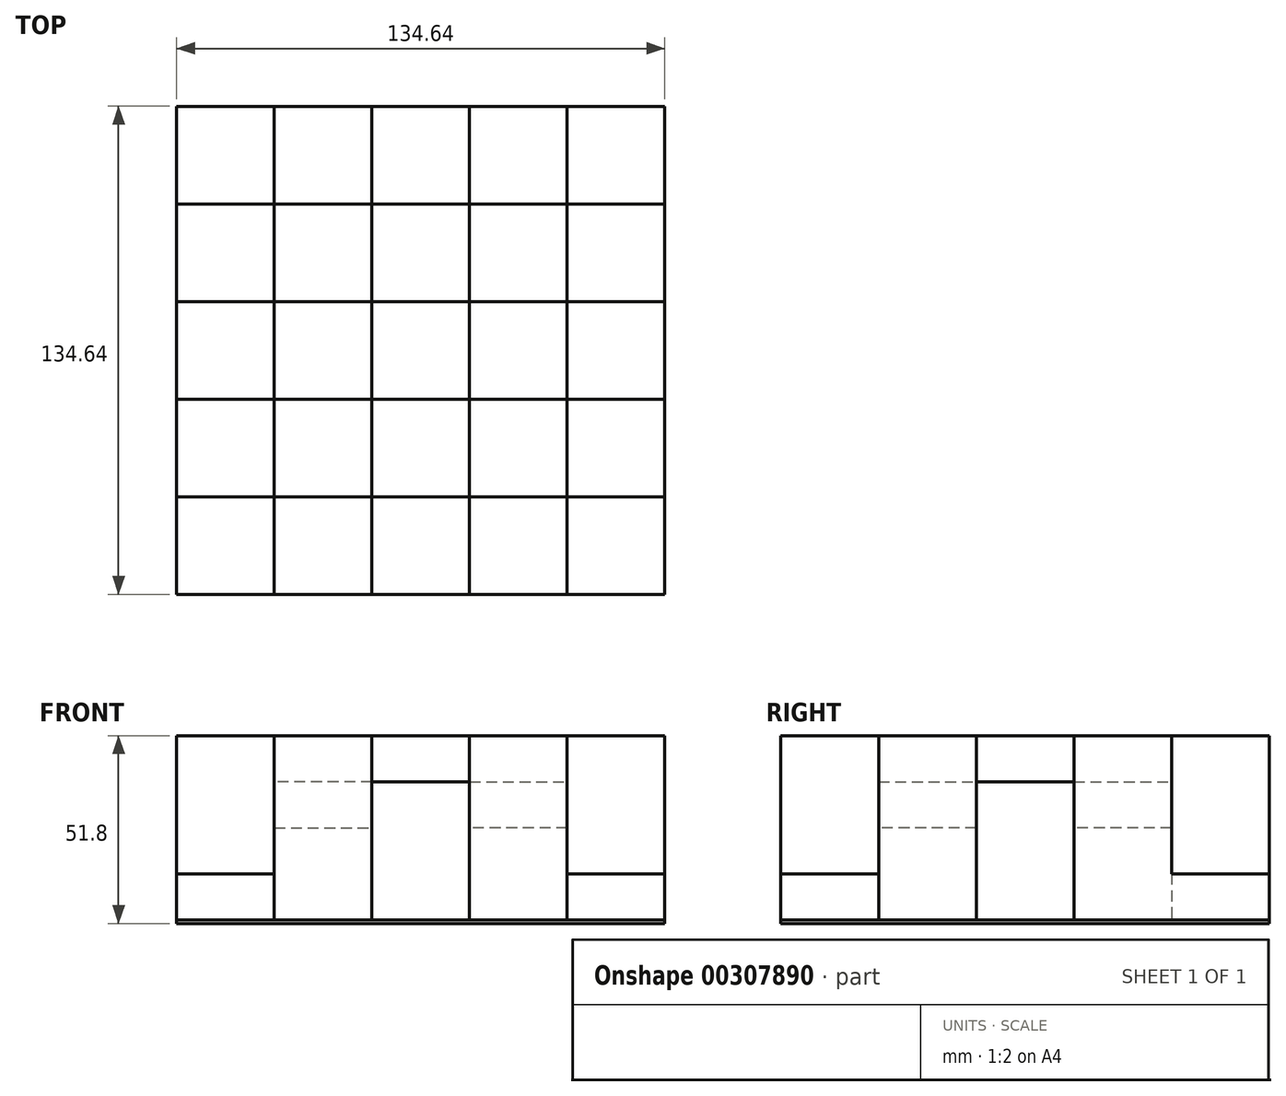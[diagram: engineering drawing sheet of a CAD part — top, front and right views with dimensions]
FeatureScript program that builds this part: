
annotation { "Feature Type Name" : "Feature", "Feature Type Description" : "" }
export const myFeature = defineFeature(function(context is Context, id is Id, definition is map)
    precondition{}
    {
        {
            var Q0;
            Q0=qCreatedBy(makeId("Top.planeOp"),FACE);
            var sketch = newSketch(context, id + "F0", { "sketchPlane" : qUnion([Q0])});
            skLineSegment(sketch, "E0.bottom", {"start": v(-67.32, 67.32) * mm, "end": v(-40.4, 67.32) * mm});
            skLineSegment(sketch, "E0.top", {"start": v(-67.32, -67.32) * mm, "end": v(67.32, -67.32) * mm});
            skLineSegment(sketch, "E0.left", {"start": v(-67.32, 67.32) * mm, "end": v(-67.32, -67.32) * mm});
            skLineSegment(sketch, "E0.right", {"start": v(67.32, 67.32) * mm, "end": v(67.32, -67.32) * mm});
            skPoint(sketch, "E0.middle", {"position": v(0, 0) * mm});
            skLineSegment(sketch, "E1", {"start": v(-40.4, 67.32) * mm, "end": v(-40.4, -67.32) * mm});
            skLineSegment(sketch, "E2", {"start": v(-13.46, 67.32) * mm, "end": v(-13.46, -67.32) * mm});
            skLineSegment(sketch, "E3", {"start": v(13.46, -67.32) * mm, "end": v(13.46, 67.32) * mm});
            skLineSegment(sketch, "E4", {"start": v(40.4, 67.32) * mm, "end": v(40.4, -67.32) * mm});
            skLineSegment(sketch, "E5", {"start": v(-40.4, 67.32) * mm, "end": v(-13.46, 67.32) * mm});
            skLineSegment(sketch, "E6", {"start": v(-13.46, 67.32) * mm, "end": v(13.46, 67.32) * mm});
            skLineSegment(sketch, "E7", {"start": v(13.46, 67.32) * mm, "end": v(40.4, 67.32) * mm});
            skLineSegment(sketch, "E8", {"start": v(40.4, 67.32) * mm, "end": v(67.32, 67.32) * mm});
            skLineSegment(sketch, "E9.1.1", {"start": v(67.32, 40.4) * mm, "end": v(-67.32, 40.4) * mm});
            skLineSegment(sketch, "E9.1.2", {"start": v(67.32, 13.46) * mm, "end": v(-67.32, 13.46) * mm});
            skLineSegment(sketch, "E9.1.3", {"start": v(-67.32, -13.46) * mm, "end": v(67.32, -13.46) * mm});
            skLineSegment(sketch, "E9.1.4", {"start": v(67.32, -40.4) * mm, "end": v(-67.32, -40.4) * mm});
            skLineSegment(sketch, "E9.anchor1", {"start": v(0, 0) * mm, "end": v(-40.4, -67.32) * mm, "construction": true});
            skLineSegment(sketch, "E9.anchor2", {"start": v(0, 0) * mm, "end": v(-67.32, 40.4) * mm, "construction": true});
            skSolve(sketch);
        }
        {
            var Q0;
            {var subQ0=sQuery(id+"F0.wireOp",EDGE,"E9.1.2");var subQ1=sQuery(id+"F0.wireOp",EDGE,"E1");var subQ2=makeQuery(id+"F0.imprint","INTERSECT",VERTEX,{"derivedFrom":[subQ1,subQ0]});Q0=makeQuery(id+"F0.imprint","IMPRINT",FACE,{"disambiguationData":[TD([[makeQuery(id+"F0.imprint","IMPRINT",EDGE,{"disambiguationData":[TD([[subQ2,-1.0]])],"derivedFrom":subQ1}),1.0]])]});}
            var Q1;
            {var subQ0=sQuery(id+"F0.wireOp",EDGE,"E9.1.1");var subQ1=sQuery(id+"F0.wireOp",EDGE,"E2");var subQ2=makeQuery(id+"F0.imprint","INTERSECT",VERTEX,{"derivedFrom":[subQ1,subQ0]});Q1=makeQuery(id+"F0.imprint","IMPRINT",FACE,{"disambiguationData":[TD([[makeQuery(id+"F0.imprint","IMPRINT",EDGE,{"disambiguationData":[TD([[subQ2,-1.0]])],"derivedFrom":subQ1}),1.0]])]});}
            var Q2;
            {var subQ0=sQuery(id+"F0.wireOp",EDGE,"E9.1.3");var subQ1=sQuery(id+"F0.wireOp",EDGE,"E3");var subQ2=makeQuery(id+"F0.imprint","INTERSECT",VERTEX,{"derivedFrom":[subQ1,subQ0]});Q2=makeQuery(id+"F0.imprint","IMPRINT",FACE,{"disambiguationData":[TD([[makeQuery(id+"F0.imprint","IMPRINT",EDGE,{"disambiguationData":[TD([[subQ2,-1.0]])],"derivedFrom":subQ1}),-1.0]])]});}
            var Q3;
            {var subQ0=sQuery(id+"F0.wireOp",EDGE,"E9.1.3");var subQ1=sQuery(id+"F0.wireOp",EDGE,"E2");var subQ2=makeQuery(id+"F0.imprint","INTERSECT",VERTEX,{"derivedFrom":[subQ1,subQ0]});Q3=makeQuery(id+"F0.imprint","IMPRINT",FACE,{"disambiguationData":[TD([[makeQuery(id+"F0.imprint","IMPRINT",EDGE,{"disambiguationData":[TD([[subQ2,-1.0]])],"derivedFrom":subQ1}),1.0]])]});}
            extrude(context, id + "F1", {"entities" : qUnion([Q0, Q1, Q2, Q3]), "depth" : 38.1 * mm});
        }
        {
            var Q0;
            {var subQ0=sQuery(id+"F0.wireOp",EDGE,"E9.1.3");var subQ1=sQuery(id+"F0.wireOp",EDGE,"E1");var subQ2=makeQuery(id+"F0.imprint","INTERSECT",VERTEX,{"derivedFrom":[subQ1,subQ0]});Q0=makeQuery(id+"F0.imprint","IMPRINT",FACE,{"disambiguationData":[TD([[makeQuery(id+"F0.imprint","IMPRINT",EDGE,{"disambiguationData":[TD([[subQ2,-1.0]])],"derivedFrom":subQ1}),1.0]])]});}
            var Q1;
            {var subQ0=sQuery(id+"F0.wireOp",EDGE,"E9.1.1");var subQ1=sQuery(id+"F0.wireOp",EDGE,"E1");var subQ2=makeQuery(id+"F0.imprint","INTERSECT",VERTEX,{"derivedFrom":[subQ1,subQ0]});Q1=makeQuery(id+"F0.imprint","IMPRINT",FACE,{"disambiguationData":[TD([[makeQuery(id+"F0.imprint","IMPRINT",EDGE,{"disambiguationData":[TD([[subQ2,-1.0]])],"derivedFrom":subQ1}),1.0]])]});}
            var Q2;
            {var subQ0=sQuery(id+"F0.wireOp",EDGE,"E9.1.2");var subQ1=sQuery(id+"F0.wireOp",EDGE,"E3");var subQ2=makeQuery(id+"F0.imprint","INTERSECT",VERTEX,{"derivedFrom":[subQ1,subQ0]});Q2=makeQuery(id+"F0.imprint","IMPRINT",FACE,{"disambiguationData":[TD([[makeQuery(id+"F0.imprint","IMPRINT",EDGE,{"disambiguationData":[TD([[subQ2,-1.0]])],"derivedFrom":subQ1}),-1.0]])]});}
            var Q3;
            {var subQ0=sQuery(id+"F0.wireOp",EDGE,"E9.1.4");var subQ1=sQuery(id+"F0.wireOp",EDGE,"E3");var subQ2=makeQuery(id+"F0.imprint","INTERSECT",VERTEX,{"derivedFrom":[subQ1,subQ0]});Q3=makeQuery(id+"F0.imprint","IMPRINT",FACE,{"disambiguationData":[TD([[makeQuery(id+"F0.imprint","IMPRINT",EDGE,{"disambiguationData":[TD([[subQ2,-1.0]])],"derivedFrom":subQ1}),-1.0]])]});}
            extrude(context, id + "F2", {"entities" : qUnion([Q0, Q1, Q2, Q3]), "depth" : 25.4 * mm});
        }
        {
            var Q0;
            {var subQ0=sQuery(id+"F0.wireOp",EDGE,"E0.bottom");Q0=makeQuery(id+"F0.imprint","IMPRINT",FACE,{"disambiguationData":[TD([[makeQuery(id+"F0.imprint","IMPRINT",EDGE,{"derivedFrom":subQ0}),-1.0]])]});}
            var Q1;
            {var subQ0=sQuery(id+"F0.wireOp",EDGE,"E0.left");var subQ1=sQuery(id+"F0.wireOp",EDGE,"E0.top");var subQ2=makeQuery(id+"F0.imprint","INTERSECT",VERTEX,{"derivedFrom":[subQ1,subQ0]});Q1=makeQuery(id+"F0.imprint","IMPRINT",FACE,{"disambiguationData":[TD([[makeQuery(id+"F0.imprint","IMPRINT",EDGE,{"disambiguationData":[TD([[subQ2,-1.0]])],"derivedFrom":subQ1}),1.0]])]});}
            var Q2;
            {var subQ0=sQuery(id+"F0.wireOp",EDGE,"E8");Q2=makeQuery(id+"F0.imprint","IMPRINT",FACE,{"disambiguationData":[TD([[makeQuery(id+"F0.imprint","IMPRINT",EDGE,{"derivedFrom":subQ0}),-1.0]])]});}
            var Q3;
            {var subQ0=sQuery(id+"F0.wireOp",EDGE,"E0.right");var subQ1=sQuery(id+"F0.wireOp",EDGE,"E0.top");var subQ2=makeQuery(id+"F0.imprint","INTERSECT",VERTEX,{"derivedFrom":[subQ1,subQ0]});Q3=makeQuery(id+"F0.imprint","IMPRINT",FACE,{"disambiguationData":[TD([[makeQuery(id+"F0.imprint","IMPRINT",EDGE,{"disambiguationData":[TD([[subQ2,1.0]])],"derivedFrom":subQ1}),1.0]])]});}
            extrude(context, id + "F3", {"entities" : qUnion([Q0, Q1, Q2, Q3]), "depth" : 12.7 * mm});
        }
        {
            var Q0;
            {var subQ0=sQuery(id+"F0.wireOp",EDGE,"E9.1.1");var subQ1=sQuery(id+"F0.wireOp",EDGE,"E0.left");var subQ2=makeQuery(id+"F0.imprint","INTERSECT",VERTEX,{"derivedFrom":[subQ1,subQ0]});Q0=makeQuery(id+"F0.imprint","IMPRINT",FACE,{"disambiguationData":[TD([[makeQuery(id+"F0.imprint","IMPRINT",EDGE,{"disambiguationData":[TD([[subQ2,-1.0]])],"derivedFrom":subQ1}),1.0]])]});}
            var Q1;
            {var subQ0=sQuery(id+"F0.wireOp",EDGE,"E5");Q1=makeQuery(id+"F0.imprint","IMPRINT",FACE,{"disambiguationData":[TD([[makeQuery(id+"F0.imprint","IMPRINT",EDGE,{"derivedFrom":subQ0}),-1.0]])]});}
            var Q2;
            {var subQ0=sQuery(id+"F0.wireOp",EDGE,"E7");Q2=makeQuery(id+"F0.imprint","IMPRINT",FACE,{"disambiguationData":[TD([[makeQuery(id+"F0.imprint","IMPRINT",EDGE,{"derivedFrom":subQ0}),-1.0]])]});}
            var Q3;
            {var subQ0=sQuery(id+"F0.wireOp",EDGE,"E9.1.1");var subQ1=sQuery(id+"F0.wireOp",EDGE,"E0.right");var subQ2=makeQuery(id+"F0.imprint","INTERSECT",VERTEX,{"derivedFrom":[subQ1,subQ0]});Q3=makeQuery(id+"F0.imprint","IMPRINT",FACE,{"disambiguationData":[TD([[makeQuery(id+"F0.imprint","IMPRINT",EDGE,{"disambiguationData":[TD([[subQ2,-1.0]])],"derivedFrom":subQ1}),-1.0]])]});}
            var Q4;
            {var subQ0=sQuery(id+"F0.wireOp",EDGE,"E9.1.3");var subQ1=sQuery(id+"F0.wireOp",EDGE,"E0.right");var subQ2=makeQuery(id+"F0.imprint","INTERSECT",VERTEX,{"derivedFrom":[subQ1,subQ0]});Q4=makeQuery(id+"F0.imprint","IMPRINT",FACE,{"disambiguationData":[TD([[makeQuery(id+"F0.imprint","IMPRINT",EDGE,{"disambiguationData":[TD([[subQ2,-1.0]])],"derivedFrom":subQ1}),-1.0]])]});}
            var Q5;
            {var subQ0=sQuery(id+"F0.wireOp",EDGE,"E3");var subQ1=sQuery(id+"F0.wireOp",EDGE,"E0.top");var subQ2=makeQuery(id+"F0.imprint","INTERSECT",VERTEX,{"derivedFrom":[subQ1,subQ0]});Q5=makeQuery(id+"F0.imprint","IMPRINT",FACE,{"disambiguationData":[TD([[makeQuery(id+"F0.imprint","IMPRINT",EDGE,{"disambiguationData":[TD([[subQ2,-1.0]])],"derivedFrom":subQ1}),1.0]])]});}
            var Q6;
            {var subQ0=sQuery(id+"F0.wireOp",EDGE,"E1");var subQ1=sQuery(id+"F0.wireOp",EDGE,"E0.top");var subQ2=makeQuery(id+"F0.imprint","INTERSECT",VERTEX,{"derivedFrom":[subQ1,subQ0]});Q6=makeQuery(id+"F0.imprint","IMPRINT",FACE,{"disambiguationData":[TD([[makeQuery(id+"F0.imprint","IMPRINT",EDGE,{"disambiguationData":[TD([[subQ2,-1.0]])],"derivedFrom":subQ1}),1.0]])]});}
            var Q7;
            {var subQ0=sQuery(id+"F0.wireOp",EDGE,"E9.1.3");var subQ1=sQuery(id+"F0.wireOp",EDGE,"E0.left");var subQ2=makeQuery(id+"F0.imprint","INTERSECT",VERTEX,{"derivedFrom":[subQ1,subQ0]});Q7=makeQuery(id+"F0.imprint","IMPRINT",FACE,{"disambiguationData":[TD([[makeQuery(id+"F0.imprint","IMPRINT",EDGE,{"disambiguationData":[TD([[subQ2,-1.0]])],"derivedFrom":subQ1}),1.0]])]});}
            var Q8;
            {var subQ0=sQuery(id+"F0.wireOp",EDGE,"E9.1.2");var subQ1=sQuery(id+"F0.wireOp",EDGE,"E2");var subQ2=makeQuery(id+"F0.imprint","INTERSECT",VERTEX,{"derivedFrom":[subQ1,subQ0]});Q8=makeQuery(id+"F0.imprint","IMPRINT",FACE,{"disambiguationData":[TD([[makeQuery(id+"F0.imprint","IMPRINT",EDGE,{"disambiguationData":[TD([[subQ2,-1.0]])],"derivedFrom":subQ1}),1.0]])]});}
            extrude(context, id + "F4", {"entities" : qUnion([Q0, Q1, Q2, Q3, Q4, Q5, Q6, Q7, Q8]), "depth" : 50.8 * mm});
        }
        {
            var Q0;
            Q0=makeQuery(id+"F4.opExtrude","SWEPT_BODY",BODY,{"disambiguationData":[OSD([sQuery(id+"F0.wireOp",EDGE,"E0.left"),sQuery(id+"F0.wireOp",EDGE,"E1"),sQuery(id+"F0.wireOp",EDGE,"E9.1.3"),sQuery(id+"F0.wireOp",EDGE,"E9.1.4")])]});
            var Q1;
            Q1=makeQuery(id+"F3.opExtrude","SWEPT_BODY",BODY,{"disambiguationData":[OSD([sQuery(id+"F0.wireOp",EDGE,"E0.top"),sQuery(id+"F0.wireOp",EDGE,"E0.left"),sQuery(id+"F0.wireOp",EDGE,"E1"),sQuery(id+"F0.wireOp",EDGE,"E9.1.4")])]});
            booleanBodies(context, id + "F5", {"operationType" : BooleanOperationType.UNION, "tools" : qUnion([Q0, Q1])});
        }
        {
            var Q0;
            Q0=makeQuery(id+"F4.opExtrude","SWEPT_BODY",BODY,{"disambiguationData":[OSD([sQuery(id+"F0.wireOp",EDGE,"E0.right"),sQuery(id+"F0.wireOp",EDGE,"E4"),sQuery(id+"F0.wireOp",EDGE,"E9.1.1"),sQuery(id+"F0.wireOp",EDGE,"E9.1.2")])]});
            var Q1;
            Q1=makeQuery(id+"F3.opExtrude","SWEPT_BODY",BODY,{"disambiguationData":[OSD([sQuery(id+"F0.wireOp",EDGE,"E0.right"),sQuery(id+"F0.wireOp",EDGE,"E4"),sQuery(id+"F0.wireOp",EDGE,"E8"),sQuery(id+"F0.wireOp",EDGE,"E9.1.1")])]});
            booleanBodies(context, id + "F6", {"operationType" : BooleanOperationType.UNION, "tools" : qUnion([Q0, Q1])});
        }
        {
            var Q0;
            {var subQ0=sQuery(id+"F0.wireOp",EDGE,"E9.1.4");var subQ1=sQuery(id+"F0.wireOp",EDGE,"E1");var subQ2=sQuery(id+"F0.wireOp",EDGE,"E0.left");Q0=makeQuery(id+"F5.opBoolean","MERGE",FACE,{"derivedFrom":[makeQuery(id+"F3.opExtrude","CAP_FACE",FACE,{"disambiguationData":[OSD([sQuery(id+"F0.wireOp",EDGE,"E0.top"),subQ2,subQ1,subQ0])],"isStart":true}),makeQuery(id+"F4.opExtrude","CAP_FACE",FACE,{"disambiguationData":[OSD([subQ2,subQ1,sQuery(id+"F0.wireOp",EDGE,"E9.1.3"),subQ0])],"isStart":true})]});}
            var sketch = newSketch(context, id + "F7", { "sketchPlane" : qUnion([Q0])});
            skLineSegment(sketch, "E10", {"start": v(67.32, -67.32) * mm, "end": v(67.32, -13.46) * mm});
            skLineSegment(sketch, "E11", {"start": v(-67.32, 13.46) * mm, "end": v(-67.32, 67.32) * mm});
            skLineSegment(sketch, "E12.bottom", {"start": v(67.32, -67.32) * mm, "end": v(-67.32, -67.32) * mm});
            skLineSegment(sketch, "E12.top", {"start": v(67.32, 67.32) * mm, "end": v(-67.32, 67.32) * mm});
            skLineSegment(sketch, "E12.left", {"start": v(67.32, -67.32) * mm, "end": v(67.32, 67.32) * mm});
            skLineSegment(sketch, "E12.right", {"start": v(-67.32, -67.32) * mm, "end": v(-67.32, 67.32) * mm});
            skSolve(sketch);
        }
        {
            var Q0;
            Q0 = qSketchRegion(id + "F7", true);
            extrude(context, id + "F8", {"entities" : qUnion([Q0]), "depth" : 1 * mm});
        }
    });
